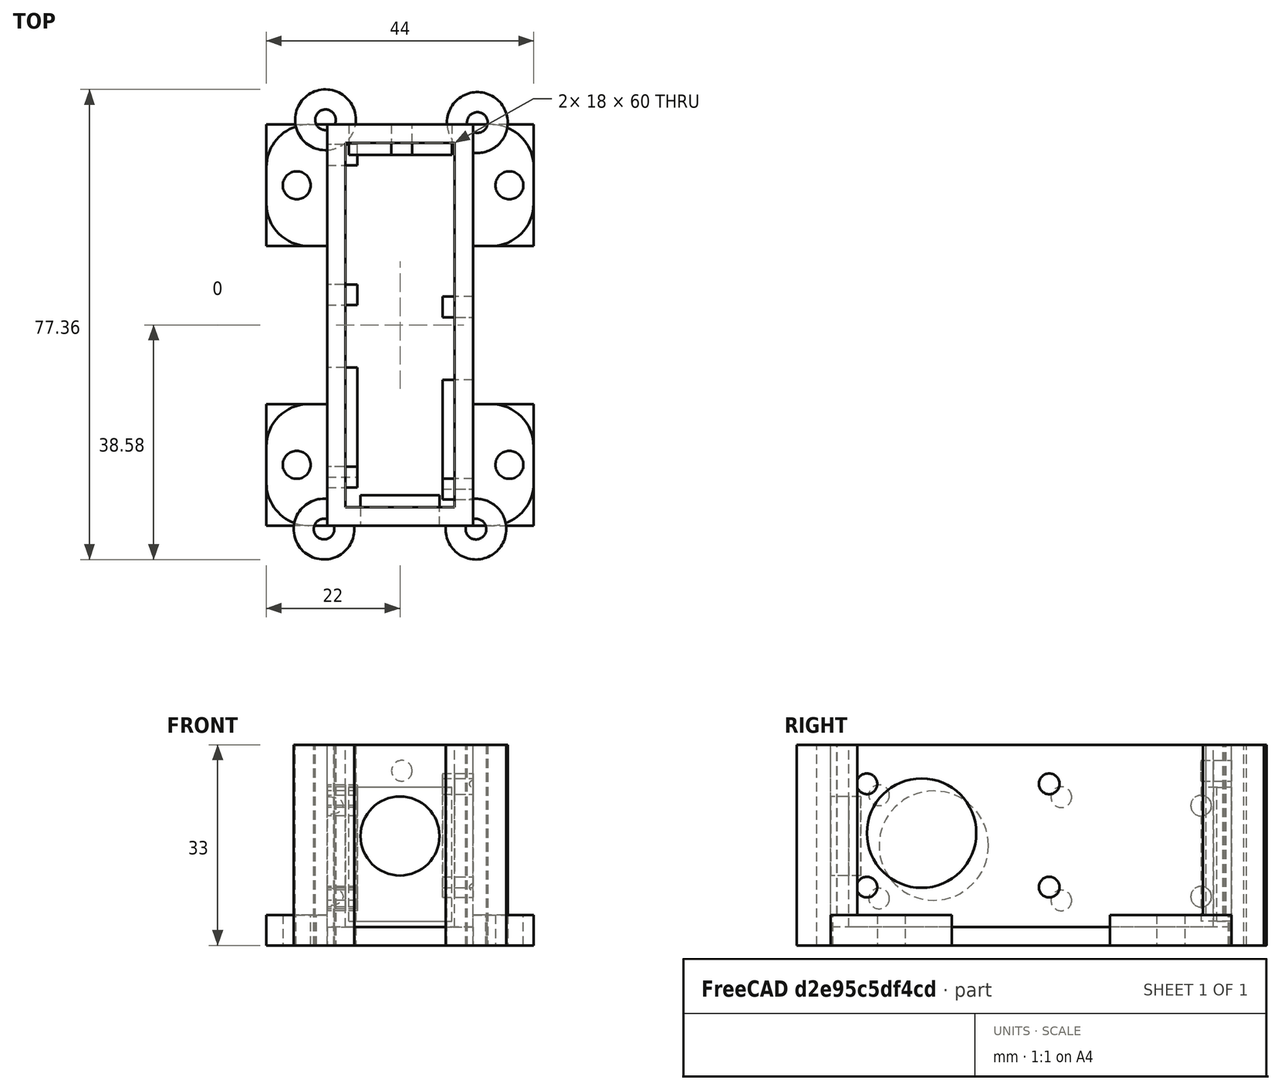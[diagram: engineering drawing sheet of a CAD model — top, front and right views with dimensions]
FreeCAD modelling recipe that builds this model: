
FCSTD DOCUMENT  (FreeCAD 0.14R2935 (Git))
Label: carcasa_modulo
License: CC-BY 3.0
LicenseURL: http://creativecommons.org/licenses/by/3.0/
objects: Sketcher::SketchObject×10, PartDesign::Pocket×6, PartDesign::Pad×4, Mesh::Feature×4, Part::Feature×1, Part::Fillet×1
note: 32 computed .brp shape members not serialized (recipe doc carries the construction recipe); baked Part::Feature solids carry a one-line shape summary decoded from their .brp

FEATURE [Sketcher::SketchObject] Sketch
  sketch-geometry (8):
    g0: LineSegment StartX=0 StartY=60 StartZ=0 EndX=18 EndY=60 EndZ=0
    g1: LineSegment StartX=18 StartY=60 StartZ=0 EndX=18 EndY=0 EndZ=0
    g2: LineSegment StartX=18 StartY=0 StartZ=0 EndX=0 EndY=0 EndZ=0
    g3: LineSegment StartX=0 StartY=0 StartZ=0 EndX=0 EndY=60 EndZ=0
    g4: LineSegment StartX=-3 StartY=63 StartZ=0 EndX=21 EndY=63 EndZ=0
    g5: LineSegment StartX=21 StartY=63 StartZ=0 EndX=21 EndY=-3 EndZ=0
    g6: LineSegment StartX=21 StartY=-3 StartZ=0 EndX=-3 EndY=-3 EndZ=0
    g7: LineSegment StartX=-3 StartY=-3 StartZ=0 EndX=-3 EndY=63 EndZ=0
  constraints (23):
    c: Coincident(g0,g1)
    c: Coincident(g1,g2)
    c: Coincident(g2,g3)
    c: Coincident(g3,g0)
    c: Horizontal(g0)
    c: Horizontal(g2)
    c: Vertical(g1)
    c: Vertical(g3)
    c: DistanceY(g1) = -60
    c: DistanceX(g0) = 18
    c: Coincident(g2,g-1)
    c: Coincident(g4,g5)
    c: Coincident(g5,g6)
    c: Coincident(g6,g7)
    c: Coincident(g7,g4)
    c: Horizontal(g4)
    c: Horizontal(g6)
    c: Vertical(g5)
    c: Vertical(g7)
    c: Distance(g0,g7) = 3
    c: Distance(g-1,g6) = 3
    c: Distance(g0,g5) = 3
    c: Distance(g0,g4) = 3
FEATURE [PartDesign::Pad] Pad
  Length = 30
  Length2 = 100
  Sketch = -> Sketch
  Type = 0
FEATURE [Sketcher::SketchObject] Sketch001
  ExternalGeometry = -> [Pad]
  Placement = pos=(0,0,0) rot=(1,0,0;3.14159rad)
  Support = -> Pad [Face9]
  sketch-geometry (4):
    g0: LineSegment StartX=-3 StartY=3 StartZ=0 EndX=21 EndY=3 EndZ=0
    g1: LineSegment StartX=21 StartY=3 StartZ=0 EndX=21 EndY=-63 EndZ=0
    g2: LineSegment StartX=21 StartY=-63 StartZ=0 EndX=-3 EndY=-63 EndZ=0
    g3: LineSegment StartX=-3 StartY=-63 StartZ=0 EndX=-3 EndY=3 EndZ=0
  constraints (11):
    c: Coincident(g0,g1)
    c: Coincident(g1,g2)
    c: Coincident(g2,g3)
    c: Coincident(g3,g0)
    c: Horizontal(g0)
    c: Horizontal(g2)
    c: Vertical(g1)
    c: Vertical(g3)
    c: Coincident(g0,g-6)
    c: Coincident(g1,g-4)
    c: Coincident(g2,g-5)
FEATURE [PartDesign::Pad] Pad001
  Length = 3
  Length2 = 100
  Sketch = -> Sketch001
  Type = 0
FEATURE [Sketcher::SketchObject] Sketch002
  ExternalGeometry = -> [Pad001]
  Placement = pos=(-3,0,0) rot=(0.57735,-0.57735,-0.57735;2.0944rad)
  Support = -> Pad001 [Face5]
  sketch-geometry (6):
    g0: Circle CenterX=-14 CenterY=13.4198 CenterZ=0 NormalX=0 NormalY=0 NormalZ=1 Radius=9
    g1: Circle CenterX=-34.9983 CenterY=21.3939 CenterZ=0 NormalX=0 NormalY=0 NormalZ=1 Radius=1.7
    g2: Circle CenterX=-34.9983 CenterY=4.39385 CenterZ=0 NormalX=0 NormalY=0 NormalZ=1 Radius=1.7
    g3: Circle CenterX=-5 CenterY=21.7118 CenterZ=0 NormalX=0 NormalY=0 NormalZ=1 Radius=1.7
    g4: Circle CenterX=-5 CenterY=4.71184 CenterZ=0 NormalX=0 NormalY=0 NormalZ=1 Radius=1.7
    g5: LineSegment [constr] StartX=-5 StartY=30 StartZ=0 EndX=-5 EndY=-3 EndZ=0
  constraints (16):
    c: Radius(g0) = 9
    c: Radius(g1) = 1.7
    c: Equal(g1,g3)
    c: Equal(g3,g4)
    c: Equal(g4,g2)
    c: Distance(g2,g4) = 30
    c: Distance(g1,g3) = 30
    c: Distance(g1,g2) = 17
    c: Distance(g3,g4) = 17
    c: Vertical(g5)
    c: Tangent(g5,g0)
    c: PointOnObject(g3,g5)
    c: PointOnObject(g4,g5)
    c: PointOnObject(g5,g-3)
    c: PointOnObject(g5,g-4)
    c: Distance(g5,g-3) = 8
FEATURE [PartDesign::Pocket] Pocket
  Length = 5
  Sketch = -> Sketch002
  Type = 0
FEATURE [Sketcher::SketchObject] Sketch003
  Placement = pos=(0,63,0) rot=(0,0.707107,0.707107;3.14159rad)
  Support = -> Pocket [Face2]
  sketch-geometry (5):
    g0: LineSegment StartX=-17.5604 StartY=23 StartZ=0 EndX=-0.56042 EndY=23 EndZ=0
    g1: LineSegment StartX=-0.56042 StartY=23 StartZ=0 EndX=-0.56042 EndY=1 EndZ=0
    g2: LineSegment StartX=-0.56042 StartY=1 StartZ=0 EndX=-17.5604 EndY=1 EndZ=0
    g3: LineSegment StartX=-17.5604 StartY=1 StartZ=0 EndX=-17.5604 EndY=23 EndZ=0
    g4: Circle CenterX=-9.2939 CenterY=25.7329 CenterZ=0 NormalX=0 NormalY=0 NormalZ=1 Radius=1.7
  constraints (12):
    c: Coincident(g0,g1)
    c: Coincident(g1,g2)
    c: Coincident(g2,g3)
    c: Coincident(g3,g0)
    c: Horizontal(g0)
    c: Horizontal(g2)
    c: Vertical(g1)
    c: Vertical(g3)
    c: DistanceY(g1) = -22
    c: DistanceX(g0) = 17
    c: DistanceY(g-1,g2) = 1
    c: Radius(g4) = 1.7
FEATURE [PartDesign::Pocket] Pocket001
  Length = 5
  Sketch = -> Sketch003
  Type = 0
FEATURE [Mesh::Feature] Arduino_Pro_Nano_or_Mini_USB
FEATURE [Sketcher::SketchObject] Sketch004
  ExternalGeometry = -> [Pocket001]
  Placement = pos=(21,0,0) rot=(0.57735,0.57735,0.57735;2.0944rad)
  Support = -> Pocket001 [Face3]
  sketch-geometry (6):
    g0: Circle CenterX=12 CenterY=15.4758 CenterZ=0 NormalX=0 NormalY=0 NormalZ=1 Radius=9
    g1: Circle CenterX=3 CenterY=23.5847 CenterZ=0 NormalX=0 NormalY=0 NormalZ=1 Radius=1.7
    g2: Circle CenterX=3 CenterY=6.58472 CenterZ=0 NormalX=0 NormalY=0 NormalZ=1 Radius=1.7
    g3: Circle CenterX=33 CenterY=23.5847 CenterZ=0 NormalX=0 NormalY=0 NormalZ=1 Radius=1.7
    g4: Circle CenterX=33 CenterY=6.58472 CenterZ=0 NormalX=0 NormalY=0 NormalZ=1 Radius=1.7
    g5: LineSegment [constr] StartX=3 StartY=30 StartZ=0 EndX=3 EndY=-3 EndZ=0
  constraints (16):
    c: Radius(g0) = 9
    c: Radius(g1) = 1.7
    c: Equal(g3,g1)
    c: Equal(g1,g2)
    c: Equal(g2,g4)
    c: DistanceY(g1,g2) = -17
    c: DistanceY(g3,g4) = -17
    c: Distance(g2,g4) = 30
    c: Distance(g1,g3) = 30
    c: Vertical(g5)
    c: Tangent(g5,g0)
    c: PointOnObject(g5,g-4)
    c: PointOnObject(g5,g-3)
    c: PointOnObject(g1,g5)
    c: PointOnObject(g2,g5)
    c: DistanceX(g-2,g5) = 3
FEATURE [PartDesign::Pocket] Pocket002
  Length = 5
  Sketch = -> Sketch004
  Type = 0
FEATURE [Sketcher::SketchObject] Sketch005
  ExternalGeometry = -> [Pocket002]
  Placement = pos=(0,-3,0) rot=(1,0,0;1.5708rad)
  Support = -> Pocket002 [Face4]
  sketch-geometry (1):
    g0: Circle CenterX=9 CenterY=15 CenterZ=0 NormalX=0 NormalY=0 NormalZ=1 Radius=6.5
  constraints (3):
    c: Radius(g0) = 6.5
    c: Distance(g0,g-3) = 15
    c: Distance(g0,g-4) = 12
FEATURE [PartDesign::Pocket] Pocket003
  Length = 5
  Sketch = -> Sketch005
  Type = 0
FEATURE [Sketcher::SketchObject] Sketch006
  ExternalGeometry = -> [Pocket003]
  Placement = pos=(-3,0,0) rot=(0.57735,-0.57735,-0.57735;2.0944rad)
  Support = -> Pocket003 [Face5]
  sketch-geometry (3):
    g0: Circle CenterX=-58 CenterY=20 CenterZ=0 NormalX=0 NormalY=0 NormalZ=1 Radius=1.7
    g1: Circle CenterX=-58 CenterY=5 CenterZ=0 NormalX=0 NormalY=0 NormalZ=1 Radius=1.7
    g2: LineSegment [constr] StartX=-58 StartY=30 StartZ=0 EndX=-58 EndY=-3 EndZ=0
  constraints (10):
    c: Radius(g0) = 1.7
    c: Equal(g1,g0)
    c: Vertical(g2)
    c: PointOnObject(g2,g-3)
    c: PointOnObject(g2,g-4)
    c: PointOnObject(g1,g2)
    c: PointOnObject(g0,g2)
    c: Distance(g-3,g2) = 5
    c: Distance(g0,g1) = 15
    c: Distance(g1,g2) = 8
FEATURE [PartDesign::Pocket] Pocket004
  Length = 5
  Sketch = -> Sketch006
  Type = 0
FEATURE [Mesh::Feature] gas_sensor
  Placement = pos=(16,37,26) rot=(0.707107,0,0.707107;3.14159rad)
FEATURE [Mesh::Feature] Buzzer
  Placement = pos=(9,4,15) rot=(1,0,0;1.5708rad)
FEATURE [Mesh::Feature] gas_sensor001
  Placement = pos=(2,39,2) rot=(0.707107,0,-0.707107;3.14159rad)
FEATURE [Sketcher::SketchObject] Sketch007
  ExternalGeometry = -> [Pocket004]
  Placement = pos=(0,0,-3) rot=(1,0,0;3.14159rad)
  Support = -> Pocket004 [Face33]
  sketch-geometry (16):
    g0: LineSegment StartX=21 StartY=3 StartZ=0 EndX=31 EndY=3 EndZ=0
    g1: LineSegment StartX=31 StartY=3 StartZ=0 EndX=31 EndY=-17 EndZ=0
    g2: LineSegment StartX=31 StartY=-17 StartZ=0 EndX=21 EndY=-17 EndZ=0
    g3: LineSegment StartX=21 StartY=-17 StartZ=0 EndX=21 EndY=3 EndZ=0
    g4: LineSegment StartX=21 StartY=-43 StartZ=0 EndX=31 EndY=-43 EndZ=0
    g5: LineSegment StartX=31 StartY=-43 StartZ=0 EndX=31 EndY=-63 EndZ=0
    g6: LineSegment StartX=31 StartY=-63 StartZ=0 EndX=21 EndY=-63 EndZ=0
    g7: LineSegment StartX=21 StartY=-63 StartZ=0 EndX=21 EndY=-43 EndZ=0
    g8: LineSegment StartX=-3 StartY=-43 StartZ=0 EndX=-13 EndY=-43 EndZ=0
    g9: LineSegment StartX=-13 StartY=-43 StartZ=0 EndX=-13 EndY=-63 EndZ=0
    g10: LineSegment StartX=-13 StartY=-63 StartZ=0 EndX=-3 EndY=-63 EndZ=0
    g11: LineSegment StartX=-3 StartY=-63 StartZ=0 EndX=-3 EndY=-43 EndZ=0
    g12: LineSegment StartX=-3 StartY=3 StartZ=0 EndX=-13 EndY=3 EndZ=0
    g13: LineSegment StartX=-13 StartY=3 StartZ=0 EndX=-13 EndY=-17 EndZ=0
    g14: LineSegment StartX=-13 StartY=-17 StartZ=0 EndX=-3 EndY=-17 EndZ=0
    g15: LineSegment StartX=-3 StartY=-17 StartZ=0 EndX=-3 EndY=3 EndZ=0
  constraints (52):
    c: Coincident(g0,g1)
    c: Coincident(g1,g2)
    c: Coincident(g2,g3)
    c: Coincident(g3,g0)
    c: Horizontal(g0)
    c: Horizontal(g2)
    c: Vertical(g1)
    c: Vertical(g3)
    c: Coincident(g4,g5)
    c: Coincident(g5,g6)
    c: Coincident(g6,g7)
    c: Coincident(g7,g4)
    c: Horizontal(g4)
    c: Horizontal(g6)
    c: Vertical(g5)
    c: Vertical(g7)
    c: Coincident(g8,g9)
    c: Coincident(g9,g10)
    c: Coincident(g10,g11)
    c: Coincident(g11,g8)
    c: Horizontal(g8)
    c: Horizontal(g10)
    c: Vertical(g9)
    c: Vertical(g11)
    c: Coincident(g12,g13)
    c: Coincident(g13,g14)
    c: Coincident(g14,g15)
    c: Coincident(g15,g12)
    c: Horizontal(g12)
    c: Horizontal(g14)
    c: Vertical(g13)
    c: Vertical(g15)
    c: Equal(g13,g9)
    c: Equal(g9,g11)
    c: Equal(g11,g7)
    c: Equal(g7,g5)
    c: Equal(g5,g1)
    c: Equal(g1,g3)
    c: Equal(g3,g15)
    c: Equal(g12,g14)
    c: Equal(g14,g8)
    c: Equal(g8,g10)
    c: Equal(g10,g6)
    c: Equal(g6,g4)
    c: Equal(g4,g2)
    c: Equal(g2,g0)
    c: DistanceY(g13) = -20
    c: DistanceX(g12) = -10
    c: Coincident(g6,g-4)
    c: Coincident(g12,g-3)
    c: Coincident(g0,g-4)
    c: Coincident(g10,g-3)
FEATURE [PartDesign::Pad] Pad002
  Length = 5
  Length2 = 100
  Reversed = true
  Sketch = -> Sketch007
  Type = 0
FEATURE [Part::Feature] Pad003
  shape: bbox 44 x 66 x 33 mm, 41 faces (baked)
FEATURE [Sketcher::SketchObject] Sketch008
  ExternalGeometry = -> [Pad003]
  Placement = pos=(0,0,-3) rot=(1,0,0;3.14159rad)
  Support = -> Pad003 [Face41]
  sketch-geometry (6):
    g0: Circle CenterX=-8 CenterY=-7 CenterZ=0 NormalX=0 NormalY=0 NormalZ=1 Radius=2.3
    g1: Circle CenterX=-8 CenterY=-53 CenterZ=0 NormalX=0 NormalY=0 NormalZ=1 Radius=2.3
    g2: Circle CenterX=27 CenterY=-7 CenterZ=0 NormalX=0 NormalY=0 NormalZ=1 Radius=2.3
    g3: Circle CenterX=27 CenterY=-53 CenterZ=0 NormalX=0 NormalY=0 NormalZ=1 Radius=2.3
    g4: LineSegment [constr] StartX=-13 StartY=-53 StartZ=0 EndX=31 EndY=-53 EndZ=0
    g5: LineSegment [constr] StartX=-13 StartY=-7 StartZ=0 EndX=31 EndY=-7 EndZ=0
  constraints (20):
    c: Radius(g0) = 2.3
    c: Equal(g1,g0)
    c: Equal(g0,g2)
    c: Equal(g2,g3)
    c: Distance(g3,g1) = 35
    c: Horizontal(g4)
    c: PointOnObject(g4,g-4)
    c: PointOnObject(g4,g-3)
    c: PointOnObject(g1,g4)
    c: PointOnObject(g3,g4)
    c: Distance(g4,g-4) = 10
    c: Distance(g0,g2) = 35
    c: Horizontal(g5)
    c: PointOnObject(g0,g5)
    c: PointOnObject(g2,g5)
    c: PointOnObject(g5,g-6)
    c: PointOnObject(g5,g-5)
    c: Distance(g-5,g5) = 10
    c: Distance(g3,g4) = 4
    c: Distance(g2,g5) = 4
FEATURE [PartDesign::Pocket] Pocket005
  Length = 5
  Sketch = -> Sketch008
  Type = 0
FEATURE [Part::Fillet] Fillet
  Base = -> Pocket005
  Edges = 8 edges r=7: [Edge12,Edge14,Edge34,Edge36,Edge80,Edge93,Edge105,Edge114]
FEATURE [Sketcher::SketchObject] Sketch009
  ExternalGeometry = -> [Fillet]
  Placement = pos=(0,0,30) rot=(0,0,1;0rad)
  Support = -> Fillet [Face6]
  sketch-geometry (8):
    g0: Circle CenterX=-3.26909 CenterY=63.7833 CenterZ=0 NormalX=0 NormalY=0 NormalZ=1 Radius=5
    g1: Circle CenterX=21.7269 CenterY=63.3332 CenterZ=0 NormalX=0 NormalY=0 NormalZ=1 Radius=5
    g2: Circle CenterX=-3.5051 CenterY=-3.56571 CenterZ=0 NormalX=0 NormalY=0 NormalZ=1 Radius=5
    g3: Circle CenterX=21.4949 CenterY=-3.5757 CenterZ=0 NormalX=0 NormalY=0 NormalZ=1 Radius=5
    g4: Circle CenterX=-3.5051 CenterY=-3.56571 CenterZ=0 NormalX=0 NormalY=0 NormalZ=1 Radius=1.7
    g5: Circle CenterX=-3.26909 CenterY=63.7833 CenterZ=0 NormalX=0 NormalY=0 NormalZ=1 Radius=1.7
    g6: Circle CenterX=21.7269 CenterY=63.3332 CenterZ=0 NormalX=0 NormalY=0 NormalZ=1 Radius=1.7
    g7: Circle CenterX=21.4949 CenterY=-3.5757 CenterZ=0 NormalX=0 NormalY=0 NormalZ=1 Radius=1.7
  constraints (18):
    c: PointOnObject(g-1,g2)
    c: PointOnObject(g-7,g0)
    c: PointOnObject(g-7,g1)
    c: Radius(g1) = 5
    c: Equal(g1,g0)
    c: Equal(g0,g2)
    c: Equal(g2,g3)
    c: Radius(g6) = 1.7
    c: Equal(g6,g5)
    c: Equal(g5,g4)
    c: Equal(g4,g7)
    c: Coincident(g6,g1)
    c: Coincident(g5,g0)
    c: Coincident(g2,g4)
    c: Coincident(g7,g3)
    c: PointOnObject(g-8,g3)
    c: Distance(g3,g2) = 25
    c: Distance(g0,g1) = 25
FEATURE [PartDesign::Pad] Pad004
  Length = 33
  Length2 = 100
  Reversed = true
  Sketch = -> Sketch009
  Type = 0
